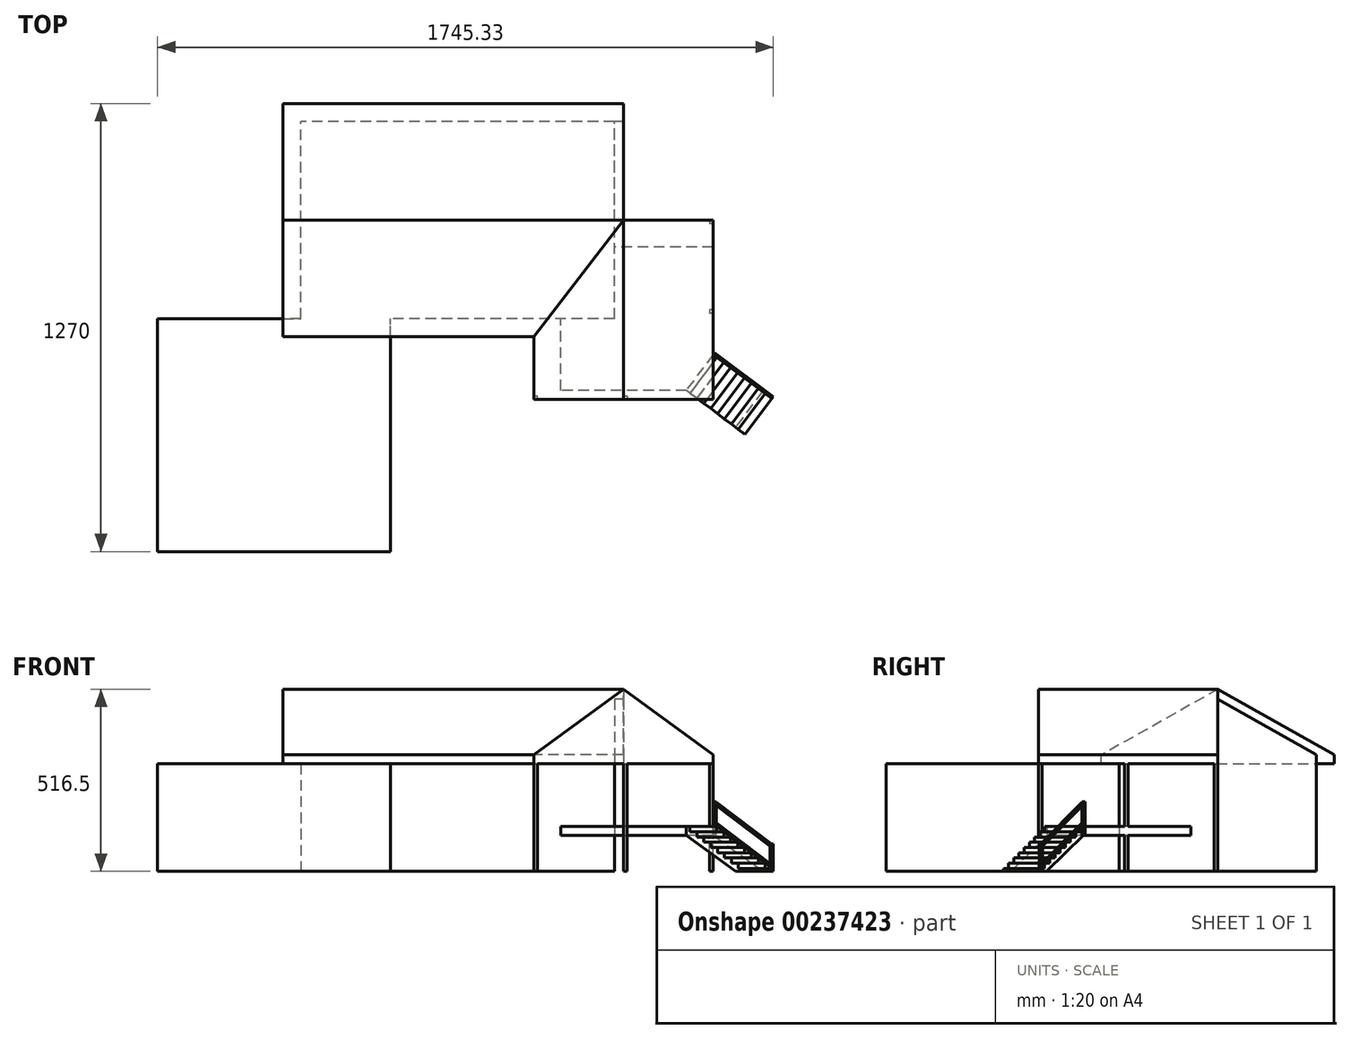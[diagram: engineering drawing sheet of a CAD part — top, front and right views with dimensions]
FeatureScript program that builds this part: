
annotation { "Feature Type Name" : "Feature", "Feature Type Description" : "" }
export const myFeature = defineFeature(function(context is Context, id is Id, definition is map)
    precondition{}
    {
        {
            var Q0;
            Q0=qCreatedBy(makeId("Right.planeOp"),FACE);
            var sketch = newSketch(context, id + "F0", { "sketchPlane" : qUnion([Q0])});
            skLineSegment(sketch, "E0.bottom", {"start": v(0, 0) * mm, "end": v(558.8, 0) * mm});
            skLineSegment(sketch, "E0.top", {"start": v(0, -304.8) * mm, "end": v(558.8, -304.8) * mm});
            skLineSegment(sketch, "E0.left", {"start": v(0, 0) * mm, "end": v(0, -304.8) * mm});
            skLineSegment(sketch, "E0.right", {"start": v(558.8, 0) * mm, "end": v(558.8, -304.8) * mm});
            skSolve(sketch);
        }
        {
            var Q0;
            Q0 = qSketchRegion(id + "F0", true);
            extrude(context, id + "F1", {"entities" : qUnion([Q0]), "depth" : 889 * mm});
        }
        {
            var Q0;
            Q0=makeQuery(id+"F1.opExtrude","CAP_FACE",FACE,{"disambiguationData":[OSD([sQuery(id+"F0.wireOp",EDGE,"E0.bottom"),sQuery(id+"F0.wireOp",EDGE,"E0.top"),sQuery(id+"F0.wireOp",EDGE,"E0.left"),sQuery(id+"F0.wireOp",EDGE,"E0.right")])],"isStart":true});
            var sketch = newSketch(context, id + "F2", { "sketchPlane" : qUnion([Q0])});
            skLineSegment(sketch, "E1", {"start": v(-558.8, 0) * mm, "end": v(-609.6, 0) * mm});
            skLineSegment(sketch, "E2", {"start": v(-609.6, 0) * mm, "end": v(-609.6, 25.4) * mm});
            skLineSegment(sketch, "E3", {"start": v(-609.6, 25.4) * mm, "end": v(-279.4, 211.55) * mm});
            skPoint(sketch, "E3.endSnap0", {"position": v(-279.4, 0) * mm});
            skLineSegment(sketch, "E4", {"start": v(0, 0) * mm, "end": v(50.8, 0) * mm});
            skLineSegment(sketch, "E5", {"start": v(50.8, 0) * mm, "end": v(50.8, 25.4) * mm});
            skLineSegment(sketch, "E6", {"start": v(50.8, 25.4) * mm, "end": v(-279.4, 211.55) * mm});
            skLineSegment(sketch, "E7", {"start": v(-558.8, 0) * mm, "end": v(0, 0) * mm});
            skSolve(sketch);
        }
        {
            var Q0;
            Q0 = qSketchRegion(id + "F2", true);
            extrude(context, id + "F3", {"entities" : qUnion([Q0]), "operationType" : NewBodyOperationType.ADD, "oppositeDirection" : true, "depth" : 889 * mm});
        }
        {
            var Q0;
            Q0=makeQuery(id+"F3.boolean.opBoolean","MERGE",FACE,{"derivedFrom":[makeQuery(id+"F1.opExtrude","CAP_FACE",FACE,{"disambiguationData":[OSD([sQuery(id+"F0.wireOp",EDGE,"E0.bottom"),sQuery(id+"F0.wireOp",EDGE,"E0.top"),sQuery(id+"F0.wireOp",EDGE,"E0.left"),sQuery(id+"F0.wireOp",EDGE,"E0.right")])],"isStart":false}),makeQuery(id+"F3.opExtrude","CAP_FACE",FACE,{"disambiguationData":[OSD([sQuery(id+"F2.wireOp",EDGE,"E1"),sQuery(id+"F2.wireOp",EDGE,"E2"),sQuery(id+"F2.wireOp",EDGE,"E3"),sQuery(id+"F2.wireOp",EDGE,"E4"),sQuery(id+"F2.wireOp",EDGE,"E5"),sQuery(id+"F2.wireOp",EDGE,"E6"),sQuery(id+"F2.wireOp",EDGE,"E7")])],"isStart":false})]});
            var sketch = newSketch(context, id + "F4", { "sketchPlane" : qUnion([Q0])});
            skLineSegment(sketch, "E8", {"start": v(-50.8, 0) * mm, "end": v(0, 0) * mm});
            skLineSegment(sketch, "E9", {"start": v(0, 0) * mm, "end": v(0, 25.4) * mm});
            skLineSegment(sketch, "E10", {"start": v(0, 25.4) * mm, "end": v(279.4, 182.91) * mm});
            skLineSegment(sketch, "E11", {"start": v(279.4, 182.91) * mm, "end": v(558.8, 25.4) * mm});
            skLineSegment(sketch, "E12", {"start": v(558.8, 25.4) * mm, "end": v(558.8, 0) * mm});
            skLineSegment(sketch, "E13", {"start": v(558.8, 0) * mm, "end": v(609.6, 0) * mm});
            skLineSegment(sketch, "E14", {"start": v(609.6, 0) * mm, "end": v(609.6, 25.4) * mm});
            skLineSegment(sketch, "E15", {"start": v(609.6, 25.4) * mm, "end": v(279.4, 211.55) * mm});
            skLineSegment(sketch, "E16", {"start": v(279.4, 211.55) * mm, "end": v(-50.8, 25.4) * mm});
            skLineSegment(sketch, "E17", {"start": v(-50.8, 25.4) * mm, "end": v(-50.8, 0) * mm});
            skSolve(sketch);
        }
        {
            var Q0;
            Q0 = qSketchRegion(id + "F4", true);
            extrude(context, id + "F5", {"entities" : qUnion([Q0]), "operationType" : NewBodyOperationType.ADD, "depth" : 25.4 * mm});
        }
        {
            var Q0;
            Q0=makeQuery(id+"F5.boolean.opBoolean","MERGE",FACE,{"derivedFrom":[makeQuery(id+"F3.opExtrude","SWEPT_FACE",FACE,{"disambiguationData":[OSD([sQuery(id+"F2.wireOp",EDGE,"E5")])]}),makeQuery(id+"F5.opExtrude","SWEPT_FACE",FACE,{"disambiguationData":[OSD([sQuery(id+"F4.wireOp",EDGE,"E17")])]})]});
            var sketch = newSketch(context, id + "F6", { "sketchPlane" : qUnion([Q0])});
            skLineSegment(sketch, "E18", {"start": v(914.4, 0) * mm, "end": v(889, 0) * mm});
            skLineSegment(sketch, "E19", {"start": v(889, 0) * mm, "end": v(660.4, 0) * mm});
            skLineSegment(sketch, "E20", {"start": v(660.4, 0) * mm, "end": v(660.4, 25.4) * mm});
            skLineSegment(sketch, "E21", {"start": v(914.4, 211.69) * mm, "end": v(660.4, 25.4) * mm});
            skLineSegment(sketch, "E22", {"start": v(914.4, 0) * mm, "end": v(1168.4, 0) * mm});
            skLineSegment(sketch, "E23", {"start": v(1168.4, 0) * mm, "end": v(1168.4, 25.4) * mm});
            skLineSegment(sketch, "E24", {"start": v(1168.4, 25.4) * mm, "end": v(914.4, 211.69) * mm});
            skSolve(sketch);
        }
        {
            var Q0;
            Q0 = qSketchRegion(id + "F6", true);
            extrude(context, id + "F7", {"entities" : qUnion([Q0]), "operationType" : NewBodyOperationType.ADD, "oppositeDirection" : true, "depth" : 330.2 * mm, "hasSecondDirection" : true, "secondDirectionOppositeDirection" : false, "secondDirectionDepth" : 177.8 * mm});
        }
        {
            var Q0;
            {var subQ0=sQuery(id+"F0.wireOp",EDGE,"E0.left");var subQ1=sQuery(id+"F2.wireOp",EDGE,"E7");var subQ4=sQuery(id+"F2.wireOp",EDGE,"E4");var subQ7=sQuery(id+"F2.wireOp",EDGE,"E1");Q0=makeQuery(id+"F7.boolean.opBoolean","MERGE",FACE,{"derivedFrom":[makeQuery(id+"F5.boolean.opBoolean","MERGE",FACE,{"derivedFrom":[makeQuery(id+"F3.boolean.opBoolean","SPLIT",FACE,{"disambiguationData":[TD([makeQuery(id+"F1.opExtrude","SWEPT_FACE",FACE,{"disambiguationData":[OSD([subQ0])]})])],"derivedFrom":makeQuery(id+"F3.opExtrude","SWEPT_FACE",FACE,{"disambiguationData":[OSD([subQ7,subQ4,subQ1])]})}),makeQuery(id+"F5.opExtrude","SWEPT_FACE",FACE,{"disambiguationData":[OSD([sQuery(id+"F4.wireOp",EDGE,"E8")])]})]}),makeQuery(id+"F7.opExtrude","SWEPT_FACE",FACE,{"disambiguationData":[OSD([sQuery(id+"F6.wireOp",EDGE,"E18"),sQuery(id+"F6.wireOp",EDGE,"E19"),sQuery(id+"F6.wireOp",EDGE,"E22")])]})]});}
            var sketch = newSketch(context, id + "F8", { "sketchPlane" : qUnion([Q0])});
            skLineSegment(sketch, "E25.bottom", {"start": v(660.4, 228.6) * mm, "end": v(670.56, 228.6) * mm});
            skLineSegment(sketch, "E25.top", {"start": v(660.4, 218.44) * mm, "end": v(670.56, 218.44) * mm});
            skLineSegment(sketch, "E25.left", {"start": v(660.4, 228.6) * mm, "end": v(660.4, 218.44) * mm});
            skLineSegment(sketch, "E25.right", {"start": v(670.56, 228.6) * mm, "end": v(670.56, 218.44) * mm});
            skLineSegment(sketch, "E26.bottom", {"start": v(1168.4, -279.4) * mm, "end": v(1158.24, -279.4) * mm});
            skLineSegment(sketch, "E26.top", {"start": v(1168.4, -269.24) * mm, "end": v(1158.24, -269.24) * mm});
            skLineSegment(sketch, "E26.left", {"start": v(1168.4, -279.4) * mm, "end": v(1168.4, -269.24) * mm});
            skLineSegment(sketch, "E26.right", {"start": v(1158.24, -279.4) * mm, "end": v(1158.24, -269.24) * mm});
            skLineSegment(sketch, "E27.bottom", {"start": v(1168.4, -25.4) * mm, "end": v(1158.24, -25.4) * mm});
            skLineSegment(sketch, "E27.top", {"start": v(1168.4, -15.24) * mm, "end": v(1158.24, -15.24) * mm});
            skLineSegment(sketch, "E27.left", {"start": v(1168.4, -25.4) * mm, "end": v(1168.4, -15.24) * mm});
            skLineSegment(sketch, "E27.right", {"start": v(1158.24, -25.4) * mm, "end": v(1158.24, -15.24) * mm});
            skLineSegment(sketch, "E28", {"start": v(914.4, 228.6) * mm, "end": v(914.4, 218.44) * mm});
            skLineSegment(sketch, "E29", {"start": v(914.4, 218.44) * mm, "end": v(924.56, 218.44) * mm});
            skLineSegment(sketch, "E30", {"start": v(924.56, 218.44) * mm, "end": v(924.56, 228.6) * mm});
            skLineSegment(sketch, "E31", {"start": v(924.56, 228.6) * mm, "end": v(914.4, 228.6) * mm});
            skSolve(sketch);
        }
        {
            var Q0;
            Q0 = qSketchRegion(id + "F8", true);
            extrude(context, id + "F9", {"entities" : qUnion([Q0]), "operationType" : NewBodyOperationType.ADD, "depth" : 304.8 * mm});
        }
        {
            var Q0;
            Q0=makeQuery(id+"F1.opExtrude","SWEPT_FACE",FACE,{"disambiguationData":[OSD([sQuery(id+"F0.wireOp",EDGE,"E0.left")])]});
            var sketch = newSketch(context, id + "F10", { "sketchPlane" : qUnion([Q0])});
            skLineSegment(sketch, "E32", {"start": v(889, 0) * mm, "end": v(889, -177.8) * mm});
            skLineSegment(sketch, "E33", {"start": v(889, -177.8) * mm, "end": v(736.6, -177.8) * mm});
            skLineSegment(sketch, "E34", {"start": v(736.6, -177.8) * mm, "end": v(736.6, -203.2) * mm});
            skLineSegment(sketch, "E35", {"start": v(736.6, -203.2) * mm, "end": v(1168.4, -203.2) * mm});
            skLineSegment(sketch, "E36", {"start": v(1168.4, -203.2) * mm, "end": v(1168.4, -177.8) * mm});
            skLineSegment(sketch, "E37", {"start": v(1168.4, -177.8) * mm, "end": v(889, -177.8) * mm});
            skSolve(sketch);
        }
        {
            var Q0;
            Q0 = qSketchRegion(id + "F10", true);
            extrude(context, id + "F11", {"entities" : qUnion([Q0]), "operationType" : NewBodyOperationType.ADD, "depth" : 203.2 * mm, "hasSecondDirection" : true, "secondDirectionOppositeDirection" : true, "secondDirectionDepth" : 203.2 * mm});
        }
        {
            var Q0;
            Q0=makeQuery(id+"F1.opExtrude","SWEPT_FACE",FACE,{"disambiguationData":[OSD([sQuery(id+"F0.wireOp",EDGE,"E0.left")])]});
            var sketch = newSketch(context, id + "F12", { "sketchPlane" : qUnion([Q0])});
            skLineSegment(sketch, "E38", {"start": v(0, 0) * mm, "end": v(254, 0) * mm});
            skLineSegment(sketch, "E39", {"start": v(254, 0) * mm, "end": v(254, -304.8) * mm});
            skLineSegment(sketch, "E40", {"start": v(254, -304.8) * mm, "end": v(-406.4, -304.8) * mm});
            skLineSegment(sketch, "E41", {"start": v(-406.4, -304.8) * mm, "end": v(-406.4, 0) * mm});
            skLineSegment(sketch, "E42", {"start": v(-406.4, 0) * mm, "end": v(0, 0) * mm});
            skSolve(sketch);
        }
        {
            var Q0;
            Q0=makeQuery(id+"F11.opExtrude","SWEPT_FACE",FACE,{"disambiguationData":[OSD([sQuery(id+"F10.wireOp",EDGE,"E33"),sQuery(id+"F10.wireOp",EDGE,"E37")])]});
            var sketch = newSketch(context, id + "F13", { "sketchPlane" : qUnion([Q0])});
            skLineSegment(sketch, "E43", {"start": v(1168.4, -203.2) * mm, "end": v(1168.4, -101.6) * mm});
            skLineSegment(sketch, "E44", {"start": v(1168.4, -203.2) * mm, "end": v(1092.2, -203.2) * mm});
            skLineSegment(sketch, "E45", {"start": v(1168.4, -101.6) * mm, "end": v(1092.2, -203.2) * mm});
            skSolve(sketch);
        }
        {
            var Q0;
            Q0 = qSketchRegion(id + "F13", true);
            extrude(context, id + "F14", {"entities" : qUnion([Q0]), "operationType" : NewBodyOperationType.REMOVE, "oppositeDirection" : true, "depth" : 25.4 * mm, "offsetDistance" : 25.4 * mm});
        }
        {
            var Q0;
            Q0=makeQuery(id+"F14.boolean.opBoolean","COPY",FACE,{"derivedFrom":makeQuery(id+"F14.opExtrude","SWEPT_FACE",FACE,{"disambiguationData":[OSD([sQuery(id+"F13.wireOp",EDGE,"E45")])]})});
            var sketch = newSketch(context, id + "F15", { "sketchPlane" : qUnion([Q0])});
            skLineSegment(sketch, "E46.bottom", {"start": v(492.76, -177.8) * mm, "end": v(499.11, -177.8) * mm});
            skLineSegment(sketch, "E46.top", {"start": v(492.76, -304.8) * mm, "end": v(499.11, -304.8) * mm});
            skLineSegment(sketch, "E46.left", {"start": v(492.76, -177.8) * mm, "end": v(492.76, -304.8) * mm});
            skLineSegment(sketch, "E46.right", {"start": v(499.11, -177.8) * mm, "end": v(499.11, -304.8) * mm});
            skSolve(sketch);
        }
        {
            var Q0;
            Q0 = qSketchRegion(id + "F15", true);
            extrude(context, id + "F16", {"entities" : qUnion([Q0]), "operationType" : NewBodyOperationType.ADD, "depth" : 304.8 * mm, "offsetDistance" : 25.4 * mm});
        }
        {
            var Q0;
            Q0=makeQuery(id+"F16.opExtrude","SWEPT_FACE",FACE,{"disambiguationData":[OSD([sQuery(id+"F15.wireOp",EDGE,"E46.left")])]});
            var sketch = newSketch(context, id + "F17", { "sketchPlane" : qUnion([Q0])});
            skLineSegment(sketch, "E47", {"start": v(995.68, -177.8) * mm, "end": v(1008.81, -177.8) * mm});
            skLineSegment(sketch, "E48", {"start": v(1008.81, -177.8) * mm, "end": v(1008.81, -192.6) * mm});
            skLineSegment(sketch, "E49", {"start": v(1008.81, -192.6) * mm, "end": v(1033.22, -192.6) * mm});
            skLineSegment(sketch, "E50", {"start": v(1033.22, -192.6) * mm, "end": v(1033.22, -207.42) * mm});
            skLineSegment(sketch, "E51", {"start": v(1033.22, -207.42) * mm, "end": v(1057.63, -207.42) * mm});
            skLineSegment(sketch, "E52", {"start": v(1057.63, -207.42) * mm, "end": v(1057.63, -222.22) * mm});
            skLineSegment(sketch, "E53", {"start": v(1057.63, -222.22) * mm, "end": v(1082.04, -222.22) * mm});
            skLineSegment(sketch, "E54", {"start": v(1082.04, -222.22) * mm, "end": v(1082.04, -237.03) * mm});
            skLineSegment(sketch, "E55", {"start": v(1082.04, -237.03) * mm, "end": v(1106.45, -237.03) * mm});
            skLineSegment(sketch, "E56", {"start": v(1106.45, -237.03) * mm, "end": v(1106.45, -251.84) * mm});
            skLineSegment(sketch, "E57", {"start": v(1106.45, -251.84) * mm, "end": v(1130.86, -251.84) * mm});
            skLineSegment(sketch, "E58", {"start": v(1130.86, -251.84) * mm, "end": v(1130.86, -266.65) * mm});
            skLineSegment(sketch, "E59", {"start": v(1130.86, -266.65) * mm, "end": v(1155.27, -266.65) * mm});
            skLineSegment(sketch, "E60", {"start": v(1155.27, -266.65) * mm, "end": v(1155.27, -281.46) * mm});
            skLineSegment(sketch, "E61", {"start": v(1155.27, -281.46) * mm, "end": v(1179.68, -281.46) * mm});
            skLineSegment(sketch, "E62", {"start": v(1179.68, -281.46) * mm, "end": v(1179.68, -296.27) * mm});
            skLineSegment(sketch, "E63", {"start": v(1179.68, -296.27) * mm, "end": v(1204.09, -296.27) * mm});
            skLineSegment(sketch, "E64", {"start": v(1204.09, -296.27) * mm, "end": v(1204.09, -304.8) * mm});
            skLineSegment(sketch, "E65", {"start": v(1204.09, -304.8) * mm, "end": v(1170.14, -304.8) * mm});
            skLineSegment(sketch, "E66", {"start": v(1170.14, -304.8) * mm, "end": v(995.68, -203.2) * mm});
            skLineSegment(sketch, "E67", {"start": v(995.68, -203.2) * mm, "end": v(995.68, -177.8) * mm});
            skSolve(sketch);
        }
        {
            var Q0;
            {var subQ0=sQuery(id+"F17.wireOp",EDGE,"E66");Q0=makeQuery(id+"F17.imprint","IMPRINT",FACE,{"disambiguationData":[TD([[makeQuery(id+"F17.imprint","IMPRINT",EDGE,{"derivedFrom":subQ0}),1.0]])]});}
            var Q1;
            {var subQ0=sQuery(id+"F17.wireOp",EDGE,"E48");Q1=makeQuery(id+"F17.imprint","IMPRINT",FACE,{"disambiguationData":[TD([[makeQuery(id+"F17.imprint","IMPRINT",EDGE,{"derivedFrom":subQ0}),1.0]])]});}
            extrude(context, id + "F18", {"entities" : qUnion([Q0, Q1]), "operationType" : NewBodyOperationType.REMOVE, "oppositeDirection" : true, "depth" : 25.4 * mm, "offsetDistance" : 25.4 * mm});
        }
        {
            var Q0;
            Q0=makeQuery(id+"F16.opExtrude","SWEPT_FACE",FACE,{"disambiguationData":[OSD([sQuery(id+"F15.wireOp",EDGE,"E46.left")])]});
            extrude(context, id + "F19", {"entities" : qUnion([Q0]), "operationType" : NewBodyOperationType.ADD, "oppositeDirection" : true, "depth" : 127 * mm, "offsetDistance" : 25.4 * mm});
        }
        {
            var Q0;
            Q0=makeQuery(id+"F19.opExtrude","CAP_FACE",FACE,{"disambiguationData":[OSD([sQuery(id+"F15.wireOp",EDGE,"E46.left")])],"isStart":false});
            var sketch = newSketch(context, id + "F20", { "sketchPlane" : qUnion([Q0])});
            skPoint(sketch, "E68.oppositeSnap0", {"position": v(-1002.25, -177.8) * mm});
            skLineSegment(sketch, "E68.bottom", {"start": v(-995.68, -203.2) * mm, "end": v(-1002.25, -203.2) * mm});
            skLineSegment(sketch, "E68.top", {"start": v(-995.68, -107.96) * mm, "end": v(-1002.25, -107.96) * mm});
            skLineSegment(sketch, "E68.left", {"start": v(-995.68, -203.2) * mm, "end": v(-995.68, -107.96) * mm});
            skLineSegment(sketch, "E68.right", {"start": v(-1002.25, -203.2) * mm, "end": v(-1002.25, -107.96) * mm});
            skSolve(sketch);
        }
        {
            var Q0;
            Q0 = qSketchRegion(id + "F20", true);
            extrude(context, id + "F21", {"entities" : qUnion([Q0]), "operationType" : NewBodyOperationType.ADD, "depth" : 6.35 * mm, "offsetDistance" : 25.4 * mm});
        }
        {
            var Q0;
            Q0=makeQuery(id+"F19.opExtrude","CAP_FACE",FACE,{"disambiguationData":[OSD([sQuery(id+"F15.wireOp",EDGE,"E46.left")])],"isStart":false});
            var sketch = newSketch(context, id + "F22", { "sketchPlane" : qUnion([Q0])});
            skLineSegment(sketch, "E69.bottom", {"start": v(-1204.09, -304.8) * mm, "end": v(-1197.74, -304.8) * mm});
            skLineSegment(sketch, "E69.top", {"start": v(-1204.09, -226.42) * mm, "end": v(-1197.74, -226.42) * mm});
            skLineSegment(sketch, "E69.left", {"start": v(-1204.09, -304.8) * mm, "end": v(-1204.09, -226.42) * mm});
            skLineSegment(sketch, "E69.right", {"start": v(-1197.74, -304.8) * mm, "end": v(-1197.74, -226.42) * mm});
            skSolve(sketch);
        }
        {
            var Q0;
            Q0 = qSketchRegion(id + "F22", true);
            extrude(context, id + "F23", {"entities" : qUnion([Q0]), "operationType" : NewBodyOperationType.ADD, "depth" : 6.35 * mm, "offsetDistance" : 25.4 * mm});
        }
        {
            var Q0;
            Q0=makeQuery(id+"F23.opExtrude","CAP_FACE",FACE,{"disambiguationData":[OSD([sQuery(id+"F22.wireOp",EDGE,"E69.bottom"),sQuery(id+"F22.wireOp",EDGE,"E69.top"),sQuery(id+"F22.wireOp",EDGE,"E69.left"),sQuery(id+"F22.wireOp",EDGE,"E69.right")])],"isStart":false});
            var sketch = newSketch(context, id + "F24", { "sketchPlane" : qUnion([Q0])});
            skLineSegment(sketch, "E70", {"start": v(-1197.74, -226.42) * mm, "end": v(-1002.13, -108) * mm});
            skLineSegment(sketch, "E71", {"start": v(-1002.13, -108) * mm, "end": v(-1002.13, -114.35) * mm});
            skLineSegment(sketch, "E72", {"start": v(-1002.13, -114.35) * mm, "end": v(-1197.74, -232.77) * mm});
            skLineSegment(sketch, "E73", {"start": v(-1197.74, -232.77) * mm, "end": v(-1197.74, -226.42) * mm});
            skSolve(sketch);
        }
        {
            var Q0;
            Q0 = qSketchRegion(id + "F24", true);
            extrude(context, id + "F25", {"entities" : qUnion([Q0]), "operationType" : NewBodyOperationType.ADD, "oppositeDirection" : true, "depth" : 6.35 * mm, "offsetDistance" : 25.4 * mm});
        }
        {
            var Q0;
            Q0=makeQuery(id+"F25.boolean.opBoolean","MERGE",FACE,{"derivedFrom":[makeQuery(id+"F21.opExtrude","CAP_FACE",FACE,{"disambiguationData":[OSD([sQuery(id+"F20.wireOp",EDGE,"E68.bottom"),sQuery(id+"F20.wireOp",EDGE,"E68.top"),sQuery(id+"F20.wireOp",EDGE,"E68.left"),sQuery(id+"F20.wireOp",EDGE,"E68.right")])],"isStart":false}),makeQuery(id+"F23.opExtrude","CAP_FACE",FACE,{"disambiguationData":[OSD([sQuery(id+"F22.wireOp",EDGE,"E69.bottom"),sQuery(id+"F22.wireOp",EDGE,"E69.top"),sQuery(id+"F22.wireOp",EDGE,"E69.left"),sQuery(id+"F22.wireOp",EDGE,"E69.right")])],"isStart":false}),makeQuery(id+"F25.opExtrude","CAP_FACE",FACE,{"disambiguationData":[OSD([sQuery(id+"F24.wireOp",EDGE,"E70"),sQuery(id+"F24.wireOp",EDGE,"E71"),sQuery(id+"F24.wireOp",EDGE,"E72"),sQuery(id+"F24.wireOp",EDGE,"E73")])],"isStart":true})]});
            var sketch = newSketch(context, id + "F26", { "sketchPlane" : qUnion([Q0])});
            skLineSegment(sketch, "E74", {"start": v(-1197.74, -285.2) * mm, "end": v(-1002.25, -166.84) * mm});
            skLineSegment(sketch, "E75", {"start": v(-1002.25, -166.84) * mm, "end": v(-1002.25, -173.2) * mm});
            skLineSegment(sketch, "E76", {"start": v(-1002.25, -173.2) * mm, "end": v(-1197.74, -291.55) * mm});
            skLineSegment(sketch, "E77", {"start": v(-1197.74, -291.55) * mm, "end": v(-1197.74, -285.2) * mm});
            skSolve(sketch);
        }
        {
            var Q0;
            Q0 = qSketchRegion(id + "F26", true);
            extrude(context, id + "F27", {"entities" : qUnion([Q0]), "oppositeDirection" : true, "depth" : 6.35 * mm, "offsetDistance" : 25.4 * mm});
        }
        {
            var Q0;
            {var subQ2=sQuery(id+"F12.wireOp",EDGE,"E41");Q0=makeQuery(id+"F12.imprint","IMPRINT",FACE,{"disambiguationData":[TD([[makeQuery(id+"F12.imprint","IMPRINT",EDGE,{"derivedFrom":subQ2}),-1.0]])]});}
            var Q1;
            Q1=makeQuery(id+"F12.imprint","IMPRINT",FACE,{"disambiguationData":[TD([[makeQuery(id+"F12.imprint","IMPRINT",EDGE,{"derivedFrom":sQuery(id+"F12.wireOp",EDGE,"E38")}),1.0]])]});
            extrude(context, id + "F28", {"entities" : qUnion([Q0, Q1]), "operationType" : NewBodyOperationType.ADD, "depth" : 660.4 * mm});
        }
        {
            var Q0;
            Q0 = qSketchRegion(id + "F2", true);
            extrude(context, id + "F30", {"entities" : qUnion([Q0]), "operationType" : NewBodyOperationType.ADD, "depth" : 50.8 * mm});
        }
    });
